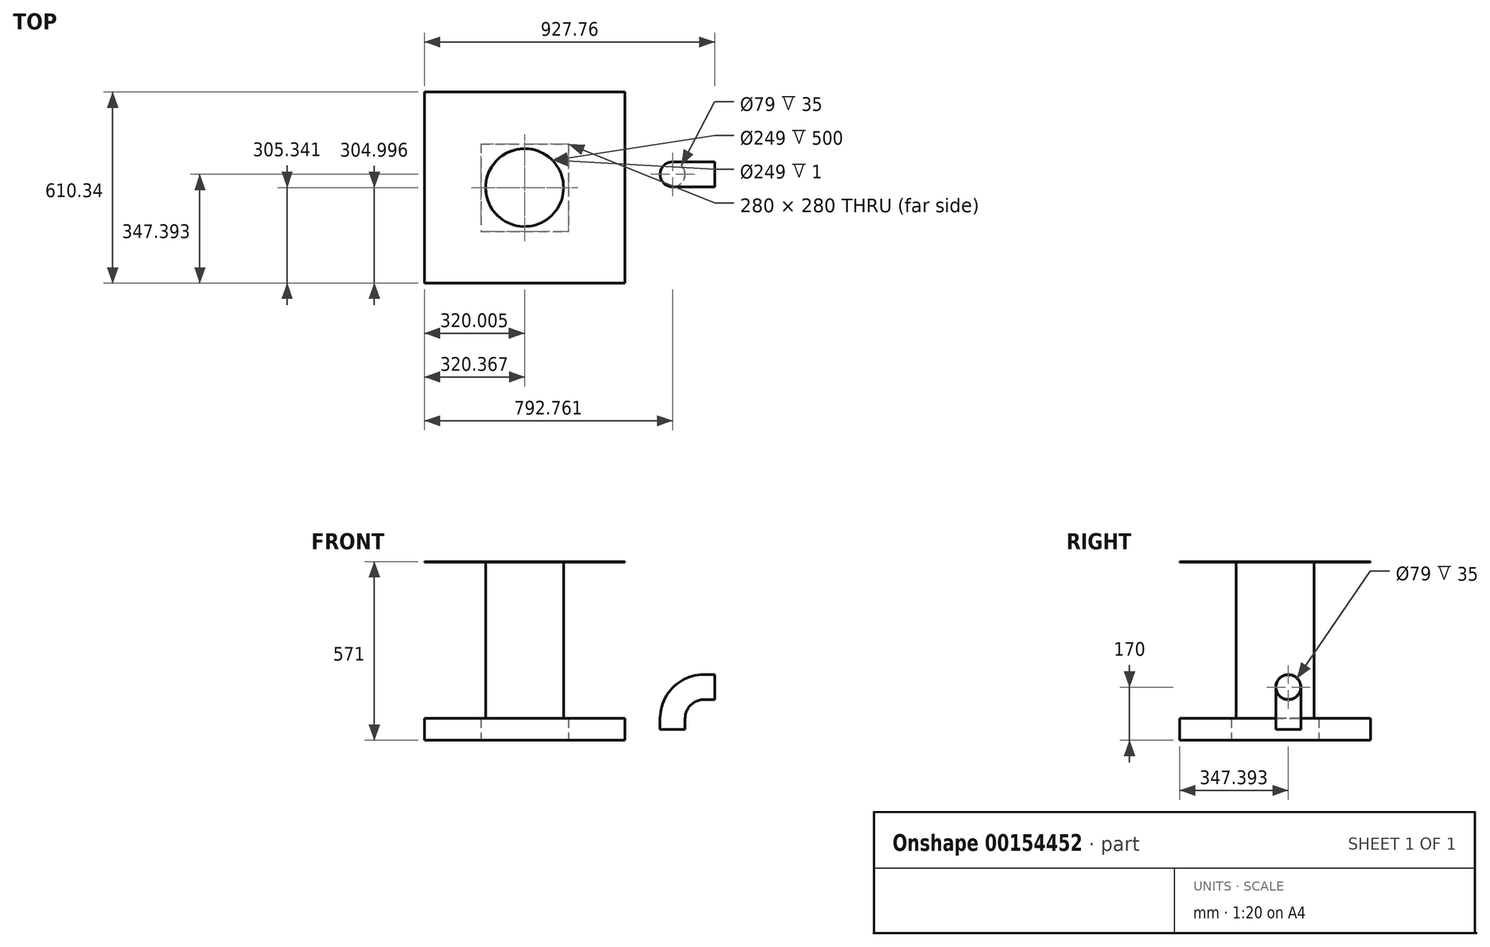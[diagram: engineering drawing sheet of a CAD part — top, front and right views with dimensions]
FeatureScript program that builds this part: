
annotation { "Feature Type Name" : "Feature", "Feature Type Description" : "" }
export const myFeature = defineFeature(function(context is Context, id is Id, definition is map)
    precondition{}
    {
        {
            var Q0;
            Q0=qCreatedBy(makeId("Top.planeOp"),FACE);
            var sketch = newSketch(context, id + "F0", { "sketchPlane" : qUnion([Q0])});
            skLineSegment(sketch, "E0.bottom", {"start": v(-267.38, 208.2) * mm, "end": v(12.62, 208.2) * mm});
            skLineSegment(sketch, "E0.top", {"start": v(-267.38, -71.8) * mm, "end": v(12.62, -71.8) * mm});
            skLineSegment(sketch, "E0.left", {"start": v(-267.38, 208.2) * mm, "end": v(-267.38, -71.8) * mm});
            skLineSegment(sketch, "E0.right", {"start": v(12.62, 208.2) * mm, "end": v(12.62, -71.8) * mm});
            skLineSegment(sketch, "E1.bottom", {"start": v(-447.38, 373.2) * mm, "end": v(192.62, 373.2) * mm});
            skLineSegment(sketch, "E1.top", {"start": v(-447.38, -236.8) * mm, "end": v(192.62, -236.8) * mm});
            skLineSegment(sketch, "E1.left", {"start": v(-447.38, 373.2) * mm, "end": v(-447.38, -236.8) * mm});
            skLineSegment(sketch, "E1.right", {"start": v(192.62, 373.2) * mm, "end": v(192.62, -236.8) * mm});
            skLineSegment(sketch, "E2", {"start": v(-127.38, 373.2) * mm, "end": v(-127.38, -236.8) * mm, "construction": true});
            skLineSegment(sketch, "E3", {"start": v(192.62, 68.2) * mm, "end": v(-447.38, 68.2) * mm, "construction": true});
            skSolve(sketch);
        }
        {
            var Q0;
            Q0 = qSketchRegion(id + "F0", true);
            extrude(context, id + "F1", {"entities" : qUnion([Q0]), "depth" : 70 * mm});
        }
        {
            var Q0;
            Q0=makeQuery(id+"F1.opExtrude","CAP_FACE",FACE,{"disambiguationData":[OSD([sQuery(id+"F0.wireOp",EDGE,"E0.bottom"),sQuery(id+"F0.wireOp",EDGE,"E0.top"),sQuery(id+"F0.wireOp",EDGE,"E0.left"),sQuery(id+"F0.wireOp",EDGE,"E0.right"),sQuery(id+"F0.wireOp",EDGE,"E1.bottom"),sQuery(id+"F0.wireOp",EDGE,"E1.top"),sQuery(id+"F0.wireOp",EDGE,"E1.left"),sQuery(id+"F0.wireOp",EDGE,"E1.right")])],"isStart":false});
            var sketch = newSketch(context, id + "F2", { "sketchPlane" : qUnion([Q0])});
            skLineSegment(sketch, "E4", {"start": v(-267.38, 68.2) * mm, "end": v(12.62, 68.2) * mm, "construction": true});
            skLineSegment(sketch, "E5", {"start": v(12.62, 68.2) * mm, "end": v(-127.38, 208.2) * mm, "construction": true});
            skLineSegment(sketch, "E6", {"start": v(-127.38, 208.2) * mm, "end": v(-127.38, -71.8) * mm, "construction": true});
            skCircle(sketch, "E7", {"center": v(-127.38, 68.2) * mm, "radius": 125 * mm});
            skCircle(sketch, "E8", {"center": v(-127.38, 68.2) * mm, "radius": 50 * mm, "construction": true});
            skCircle(sketch, "E9", {"center": v(-127.38, 68.2) * mm, "radius": 124.5 * mm});
            skSolve(sketch);
        }
        {
            var Q0;
            Q0 = qSketchRegion(id + "F2", true);
            var Q1;
            Q1=sQuery(id+"F2.wireOp",EDGE,"E7");
            var Q2;
            Q2=sQuery(id+"F2.wireOp",EDGE,"E9");
            extrude(context, id + "F3", {"entities" : qUnion([Q0]), "surfaceEntities" : qUnion([Q1, Q2]), "depth" : 500 * mm});
        }
        {
            var Q0;
            Q0=makeQuery(id+"F1.opExtrude","CAP_FACE",FACE,{"disambiguationData":[OSD([sQuery(id+"F0.wireOp",EDGE,"E0.bottom"),sQuery(id+"F0.wireOp",EDGE,"E0.top"),sQuery(id+"F0.wireOp",EDGE,"E0.left"),sQuery(id+"F0.wireOp",EDGE,"E0.right"),sQuery(id+"F0.wireOp",EDGE,"E1.bottom"),sQuery(id+"F0.wireOp",EDGE,"E1.top"),sQuery(id+"F0.wireOp",EDGE,"E1.left"),sQuery(id+"F0.wireOp",EDGE,"E1.right")])],"isStart":false});
            var sketch = newSketch(context, id + "F4", { "sketchPlane" : qUnion([Q0])});
            skCircle(sketch, "E10", {"center": v(345.01, 110.6) * mm, "radius": 40 * mm});
            skCircle(sketch, "E11", {"center": v(345.01, 110.6) * mm, "radius": 39.5 * mm});
            skLineSegment(sketch, "E12", {"start": v(445.01, 162.87) * mm, "end": v(445.01, 58.01) * mm, "construction": true});
            skSolve(sketch);
        }
        {
            var Q0;
            Q0 = qSketchRegion(id + "F4", true);
            var Q1;
            Q1=sQuery(id+"F4.wireOp",EDGE,"E12");
            revolve(context, id + "F5", {"entities" : qUnion([Q0]), "axis" : qUnion([Q1]), "revolveType" : RevolveType.ONE_DIRECTION, "oppositeDirection" : true, "angle" : 90 * degree});
        }
        {
            var Q0;
            Q0=makeQuery(id+"F5.opRevolve","CAP_FACE",FACE,{"disambiguationData":[OSD([sQuery(id+"F4.wireOp",EDGE,"E10"),sQuery(id+"F4.wireOp",EDGE,"E11")])],"isStart":false});
            var sketch = newSketch(context, id + "F6", { "sketchPlane" : qUnion([Q0])});
            skCircle(sketch, "E13", {"center": v(110.6, 170) * mm, "radius": 39.5 * mm});
            skCircle(sketch, "E14", {"center": v(110.6, 170) * mm, "radius": 40 * mm});
            skSolve(sketch);
        }
        {
            var Q0;
            Q0 = qSketchRegion(id + "F6", true);
            extrude(context, id + "F7", {"entities" : qUnion([Q0]), "operationType" : NewBodyOperationType.ADD, "depth" : 35 * mm});
        }
        {
            var Q0;
            Q0=makeQuery(id+"F5.opRevolve","CAP_FACE",FACE,{"disambiguationData":[OSD([sQuery(id+"F4.wireOp",EDGE,"E10"),sQuery(id+"F4.wireOp",EDGE,"E11")])],"isStart":true});
            var sketch = newSketch(context, id + "F8", { "sketchPlane" : qUnion([Q0])});
            skCircle(sketch, "E15", {"center": v(345.01, -110.6) * mm, "radius": 39.5 * mm});
            skCircle(sketch, "E16", {"center": v(345.01, -110.6) * mm, "radius": 40 * mm});
            skSolve(sketch);
        }
        {
            var Q0;
            Q0 = qSketchRegion(id + "F8", true);
            extrude(context, id + "F9", {"entities" : qUnion([Q0]), "operationType" : NewBodyOperationType.ADD, "depth" : 35 * mm});
        }
        {
            var Q0;
            Q0=makeQuery(id+"F3.opExtrude","CAP_FACE",FACE,{"disambiguationData":[OSD([sQuery(id+"F2.wireOp",EDGE,"E7"),sQuery(id+"F2.wireOp",EDGE,"E9")])],"isStart":false});
            var sketch = newSketch(context, id + "F10", { "sketchPlane" : qUnion([Q0])});
            skLineSegment(sketch, "E17.bottom", {"start": v(-447.75, 373.54) * mm, "end": v(192.25, 373.54) * mm});
            skLineSegment(sketch, "E17.top", {"start": v(-447.75, -236.46) * mm, "end": v(192.25, -236.46) * mm});
            skLineSegment(sketch, "E17.left", {"start": v(-447.75, 373.54) * mm, "end": v(-447.75, -236.46) * mm});
            skLineSegment(sketch, "E17.right", {"start": v(192.25, 373.54) * mm, "end": v(192.25, -236.46) * mm});
            skLineSegment(sketch, "E18", {"start": v(-447.75, 373.54) * mm, "end": v(192.25, -236.46) * mm, "construction": true});
            skLineSegment(sketch, "E19", {"start": v(192.25, 373.54) * mm, "end": v(-447.75, -236.46) * mm, "construction": true});
            skCircle(sketch, "E20", {"center": v(-127.75, 68.54) * mm, "radius": 124.5 * mm});
            skSolve(sketch);
        }
        {
            var Q0;
            Q0 = qSketchRegion(id + "F10", true);
            extrude(context, id + "F11", {"entities" : qUnion([Q0]), "operationType" : NewBodyOperationType.ADD, "depth" : 1 * mm});
        }
    });
